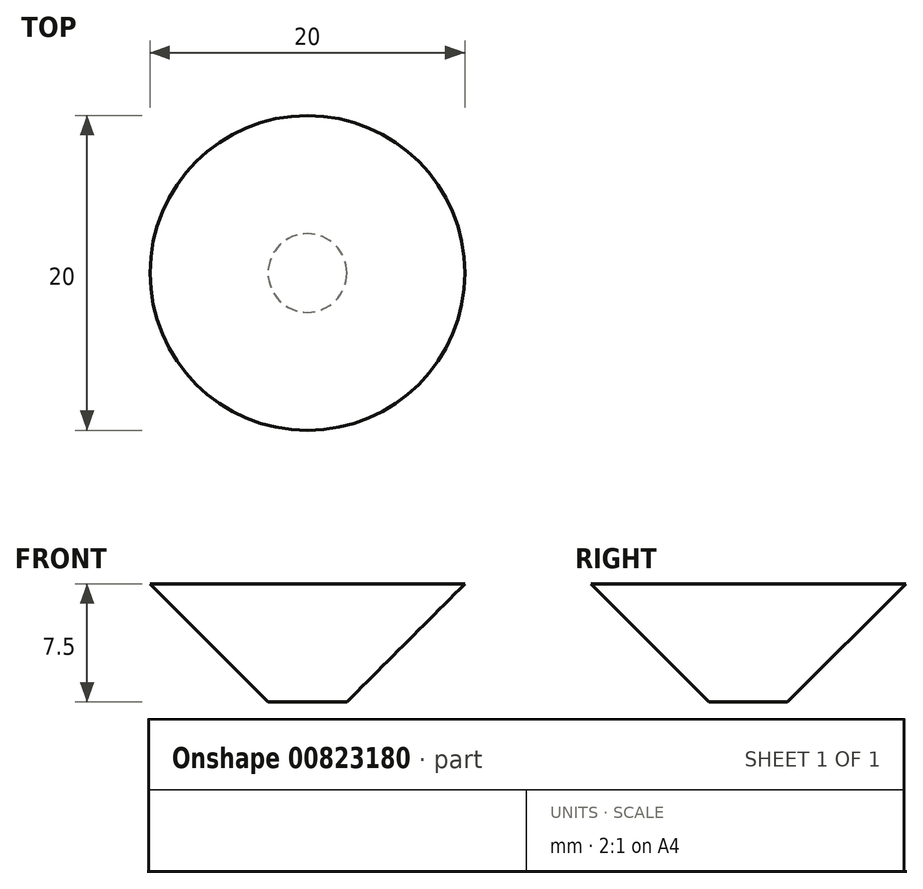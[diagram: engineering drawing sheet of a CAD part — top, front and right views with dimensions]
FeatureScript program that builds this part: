
annotation { "Feature Type Name" : "Feature", "Feature Type Description" : "" }
export const myFeature = defineFeature(function(context is Context, id is Id, definition is map)
    precondition{}
    {
        {
            var Q0;
            Q0=qCreatedBy(makeId("Front.planeOp"),FACE);
            var sketch = newSketch(context, id + "F0", { "sketchPlane" : qUnion([Q0])});
            skLineSegment(sketch, "E0", {"start": v(2.5, 2.5) * mm, "end": v(10, 10) * mm});
            skLineSegment(sketch, "E1", {"start": v(10, 10) * mm, "end": v(0, 10) * mm});
            skLineSegment(sketch, "E2", {"start": v(0, 10) * mm, "end": v(0, 2.5) * mm});
            skLineSegment(sketch, "E3", {"start": v(0, 11.75) * mm, "end": v(0, 2.5) * mm, "construction": true});
            skLineSegment(sketch, "E4", {"start": v(0, 2.5) * mm, "end": v(2.5, 2.5) * mm});
            skLineSegment(sketch, "E5.trimOffspring", {"start": v(0, 0) * mm, "end": v(0, -10.38) * mm, "construction": true});
            skSolve(sketch);
        }
        {
            var Q0;
            Q0 = qSketchRegion(id + "F0", true);
            var Q1;
            Q1=sQuery(id+"F0.wireOp",EDGE,"E3");
            revolve(context, id + "F1", {"surfaceOperationType" : NewSurfaceOperationType.NEW, "entities" : qUnion([Q0]), "axis" : qUnion([Q1]), "revolveType" : RevolveType.FULL});
        }
    });
